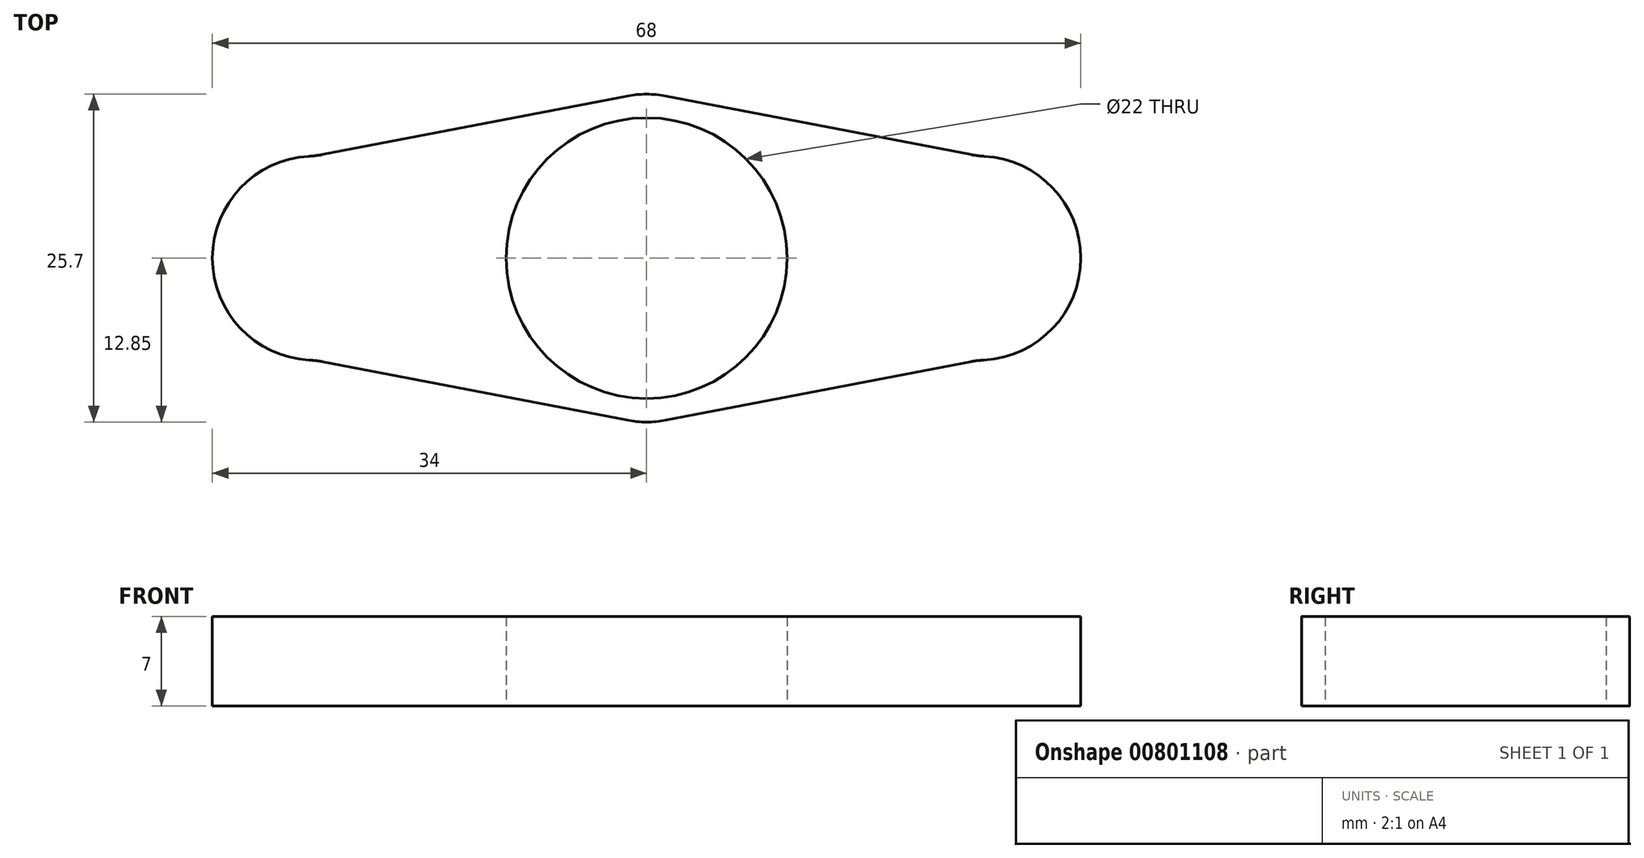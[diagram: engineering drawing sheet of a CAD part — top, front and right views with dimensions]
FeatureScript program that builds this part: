
annotation { "Feature Type Name" : "Feature", "Feature Type Description" : "" }
export const myFeature = defineFeature(function(context is Context, id is Id, definition is map)
    precondition{}
    {
        {
            var Q0;
            Q0=qCreatedBy(makeId("Top.planeOp"),FACE);
            var sketch = newSketch(context, id + "F0", { "sketchPlane" : qUnion([Q0])});
            skCircle(sketch, "E0", {"center": v(0, 0) * mm, "radius": 11 * mm});
            skCircle(sketch, "E1", {"center": v(0, 0) * mm, "radius": 13 * mm});
            skPoint(sketch, "E2", {"position": v(26, 0) * mm});
            skPoint(sketch, "E3", {"position": v(-26, 0) * mm});
            skCircle(sketch, "E4", {"center": v(-26, 0) * mm, "radius": 8 * mm});
            skCircle(sketch, "E5", {"center": v(26, 0) * mm, "radius": 8 * mm});
            skPoint(sketch, "E6", {"position": v(-26, 8) * mm});
            skPoint(sketch, "E7", {"position": v(-26, -8) * mm});
            skPoint(sketch, "E8", {"position": v(26, 8) * mm});
            skPoint(sketch, "E9", {"position": v(26, -8) * mm});
            skPoint(sketch, "E10", {"position": v(0, 13) * mm});
            skPoint(sketch, "E11", {"position": v(0, -13) * mm});
            skLineSegment(sketch, "E12", {"start": v(-26, 8) * mm, "end": v(0, 13) * mm});
            skLineSegment(sketch, "E13", {"start": v(-26, -8) * mm, "end": v(0, -13) * mm});
            skLineSegment(sketch, "E14", {"start": v(0, -13) * mm, "end": v(26, -8) * mm});
            skLineSegment(sketch, "E15", {"start": v(0, 13) * mm, "end": v(26, 8) * mm});
            skSolve(sketch);
        }
        {
            var Q0;
            {var subQ0=sQuery(id+"F0.wireOp",EDGE,"E4");var subQ1=makeQuery(id+"F0.imprint","INTERSECT",VERTEX,{"derivedFrom":[subQ0,sQuery(id+"F0.wireOp",EDGE,"E12")]});Q0=makeQuery(id+"F0.imprint","IMPRINT",FACE,{"disambiguationData":[TD([[makeQuery(id+"F0.imprint","IMPRINT",EDGE,{"disambiguationData":[TD([[subQ1,-1.0]])],"derivedFrom":subQ0}),1.0]])]});}
            var Q1;
            {var subQ0=sQuery(id+"F0.wireOp",EDGE,"E12");var subQ1=sQuery(id+"F0.wireOp",EDGE,"E1");var subQ2=makeQuery(id+"F0.imprint","INTERSECT",VERTEX,{"derivedFrom":[subQ1,subQ0]});Q1=makeQuery(id+"F0.imprint","IMPRINT",FACE,{"disambiguationData":[TD([[makeQuery(id+"F0.imprint","IMPRINT",EDGE,{"disambiguationData":[TD([[subQ2,-1.0]])],"derivedFrom":subQ1}),-1.0]])]});}
            var Q2;
            Q2=makeQuery(id+"F0.imprint","IMPRINT",FACE,{"disambiguationData":[TD([[makeQuery(id+"F0.imprint","IMPRINT",EDGE,{"derivedFrom":sQuery(id+"F0.wireOp",EDGE,"E0")}),-1.0]])]});
            var Q3;
            {var subQ0=sQuery(id+"F0.wireOp",EDGE,"E15");var subQ1=sQuery(id+"F0.wireOp",EDGE,"E1");var subQ2=makeQuery(id+"F0.imprint","INTERSECT",VERTEX,{"derivedFrom":[subQ1,subQ0]});Q3=makeQuery(id+"F0.imprint","IMPRINT",FACE,{"disambiguationData":[TD([[makeQuery(id+"F0.imprint","IMPRINT",EDGE,{"disambiguationData":[TD([[subQ2,1.0]])],"derivedFrom":subQ1}),-1.0]])]});}
            var Q4;
            {var subQ0=sQuery(id+"F0.wireOp",EDGE,"E5");var subQ1=makeQuery(id+"F0.imprint","INTERSECT",VERTEX,{"derivedFrom":[subQ0,sQuery(id+"F0.wireOp",EDGE,"E14")]});Q4=makeQuery(id+"F0.imprint","IMPRINT",FACE,{"disambiguationData":[TD([[makeQuery(id+"F0.imprint","IMPRINT",EDGE,{"disambiguationData":[TD([[subQ1,1.0]])],"derivedFrom":subQ0}),1.0]])]});}
            extrude(context, id + "F1", {"entities" : qUnion([Q0, Q1, Q2, Q3, Q4]), "depth" : 7 * mm, "offsetDistance" : 25 * mm});
        }
        {
            var Q0;
            Q0=makeQuery(id+"F1.opExtrude","SWEPT_EDGE",EDGE,{"disambiguationData":[OSD([sQuery(id+"F0.wireOp",EDGE,"E1"),sQuery(id+"F0.wireOp",EDGE,"E13"),sQuery(id+"F0.wireOp",EDGE,"E14")])]});
            var Q1;
            Q1=makeQuery(id+"F1.opExtrude","SWEPT_EDGE",EDGE,{"disambiguationData":[OSD([sQuery(id+"F0.wireOp",EDGE,"E1"),sQuery(id+"F0.wireOp",EDGE,"E12"),sQuery(id+"F0.wireOp",EDGE,"E15")])]});
            fillet(context, id + "F2", {"entities" : qUnion([Q0, Q1]), "radius" : 8 * mm, "tangentPropagation" : true, "allowEdgeOverflow" : false});
        }
        {
            var Q0;
            Q0=makeQuery(id+"F1.opExtrude","SWEPT_EDGE",EDGE,{"disambiguationData":[OSD([sQuery(id+"F0.wireOp",EDGE,"E4"),sQuery(id+"F0.wireOp",EDGE,"E13")])]});
            var Q1;
            Q1=makeQuery(id+"F1.opExtrude","SWEPT_EDGE",EDGE,{"disambiguationData":[OSD([sQuery(id+"F0.wireOp",EDGE,"E4"),sQuery(id+"F0.wireOp",EDGE,"E12")])]});
            var Q2;
            Q2=makeQuery(id+"F1.opExtrude","SWEPT_EDGE",EDGE,{"disambiguationData":[OSD([sQuery(id+"F0.wireOp",EDGE,"E5"),sQuery(id+"F0.wireOp",EDGE,"E15")])]});
            var Q3;
            Q3=makeQuery(id+"F1.opExtrude","SWEPT_EDGE",EDGE,{"disambiguationData":[OSD([sQuery(id+"F0.wireOp",EDGE,"E5"),sQuery(id+"F0.wireOp",EDGE,"E14")])]});
            fillet(context, id + "F3", {"entities" : qUnion([Q0, Q1, Q2, Q3]), "radius" : 8 * mm, "tangentPropagation" : true, "allowEdgeOverflow" : false});
        }
    });
